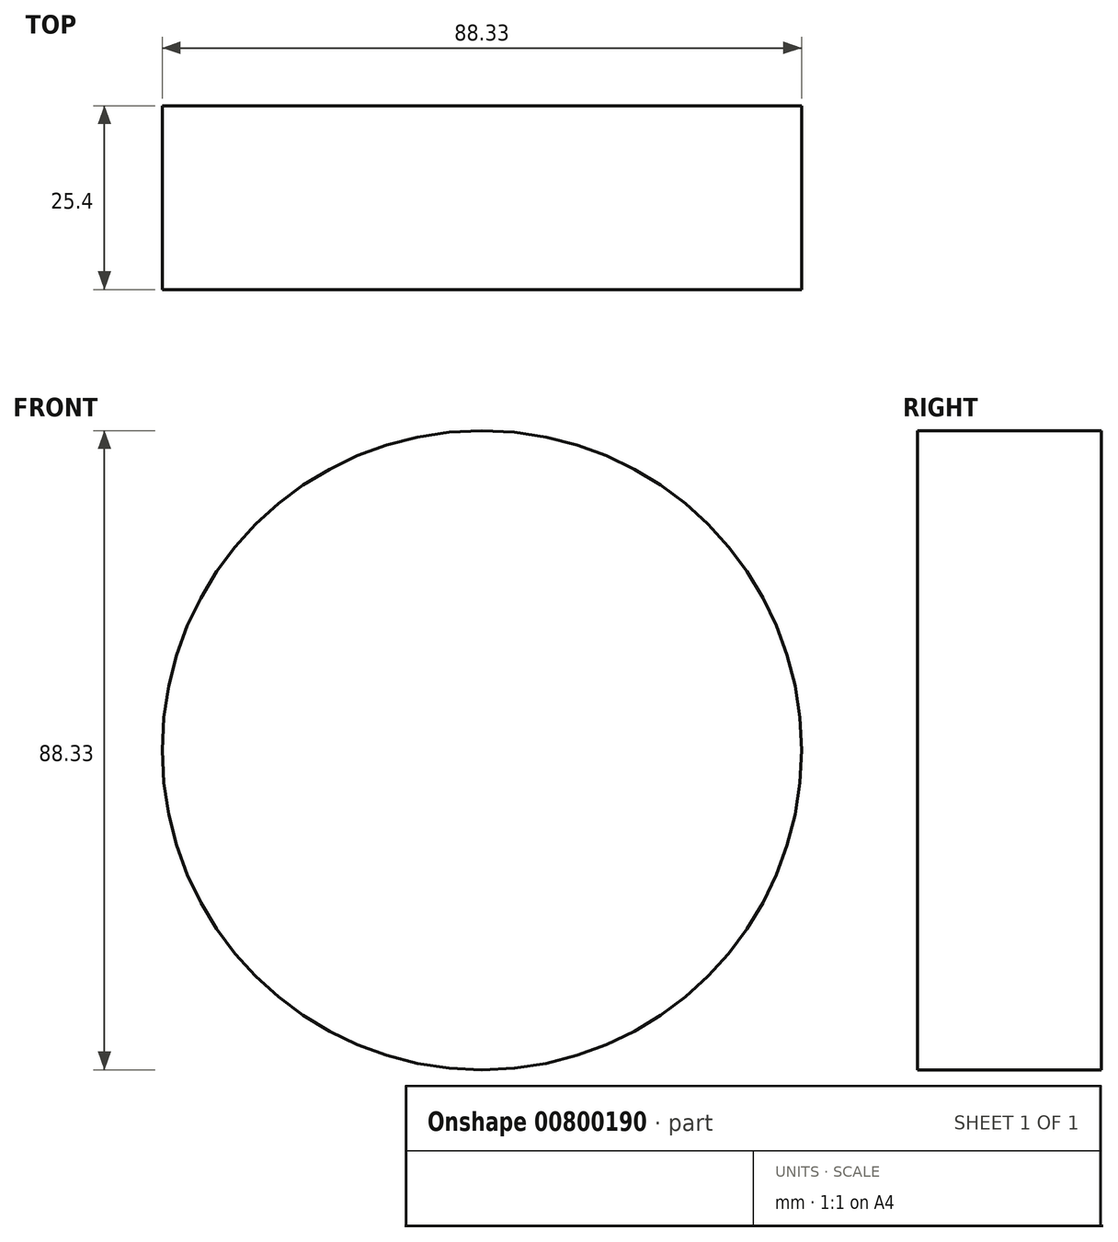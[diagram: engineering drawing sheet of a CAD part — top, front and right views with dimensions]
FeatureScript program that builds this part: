
annotation { "Feature Type Name" : "Feature", "Feature Type Description" : "" }
export const myFeature = defineFeature(function(context is Context, id is Id, definition is map)
    precondition{}
    {
        {
            var Q0;
            Q0=qCreatedBy(makeId("Front.planeOp"),FACE);
            var sketch = newSketch(context, id + "F0", { "sketchPlane" : qUnion([Q0])});
            skCircle(sketch, "E0", {"center": v(103.13, 57.28) * mm, "radius": 44.17 * mm});
            skSolve(sketch);
        }
        {
            var Q0;
            Q0=sQuery(id+"F0.wireOp",EDGE,"E0");
            extrude(context, id + "F1", {"bodyType" : ToolBodyType.SURFACE, "surfaceEntities" : qUnion([Q0]), "depth" : 25.4 * mm, "offsetDistance" : 25.4 * mm});
        }
    });
